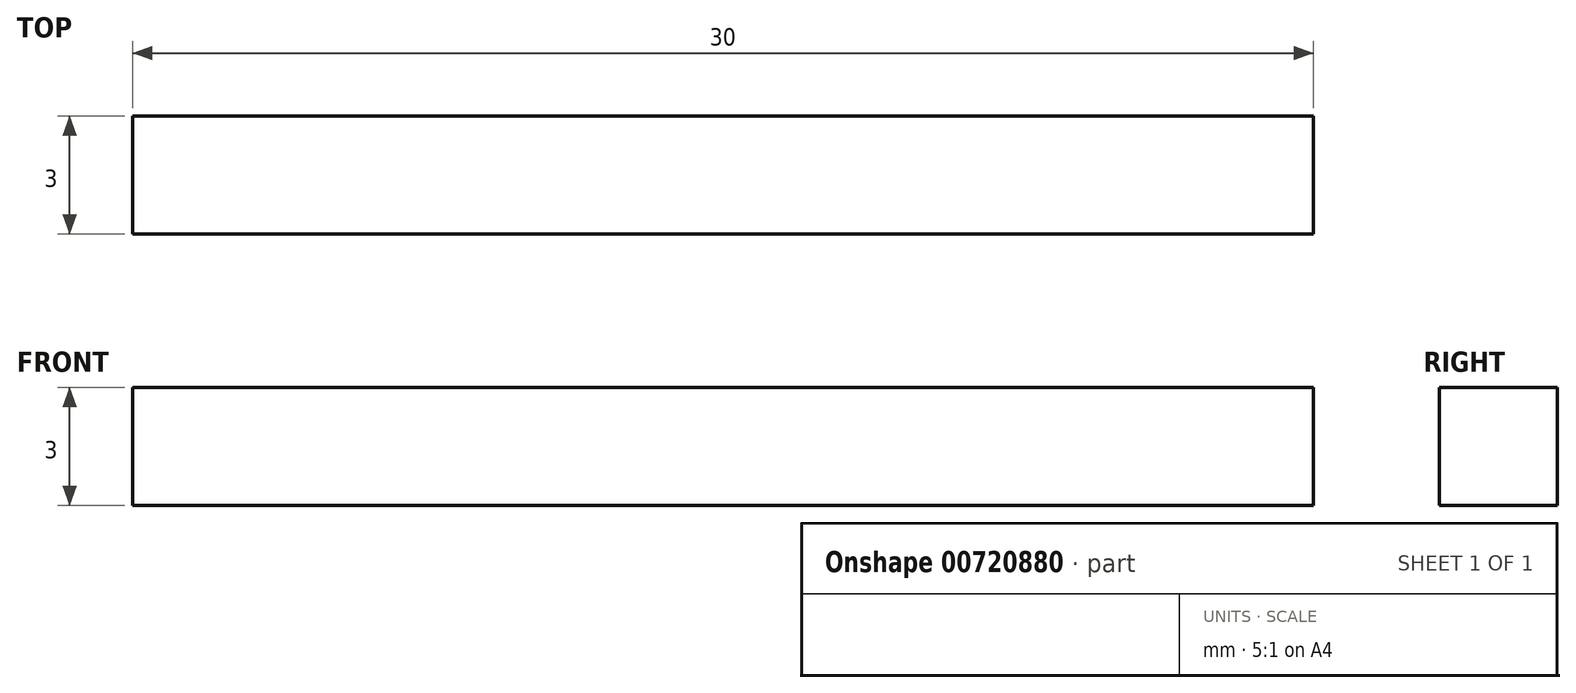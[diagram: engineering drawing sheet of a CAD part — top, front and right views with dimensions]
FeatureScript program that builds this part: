
annotation { "Feature Type Name" : "Feature", "Feature Type Description" : "" }
export const myFeature = defineFeature(function(context is Context, id is Id, definition is map)
    precondition{}
    {
        {
            var Q0;
            Q0=qCreatedBy(makeId("Top.planeOp"),FACE);
            var sketch = newSketch(context, id + "F0", { "sketchPlane" : qUnion([Q0])});
            skLineSegment(sketch, "E0.bottom", {"start": v(-15, 1.5) * mm, "end": v(15, 1.5) * mm});
            skLineSegment(sketch, "E0.top", {"start": v(-15, -1.5) * mm, "end": v(15, -1.5) * mm});
            skLineSegment(sketch, "E0.left", {"start": v(-15, 1.5) * mm, "end": v(-15, -1.5) * mm});
            skLineSegment(sketch, "E0.right", {"start": v(15, 1.5) * mm, "end": v(15, -1.5) * mm});
            skSolve(sketch);
        }
        {
            var Q0;
            Q0 = qSketchRegion(id + "F0", true);
            extrude(context, id + "F1", {"entities" : qUnion([Q0]), "depth" : 3 * mm, "offsetDistance" : 25 * mm});
        }
    });
